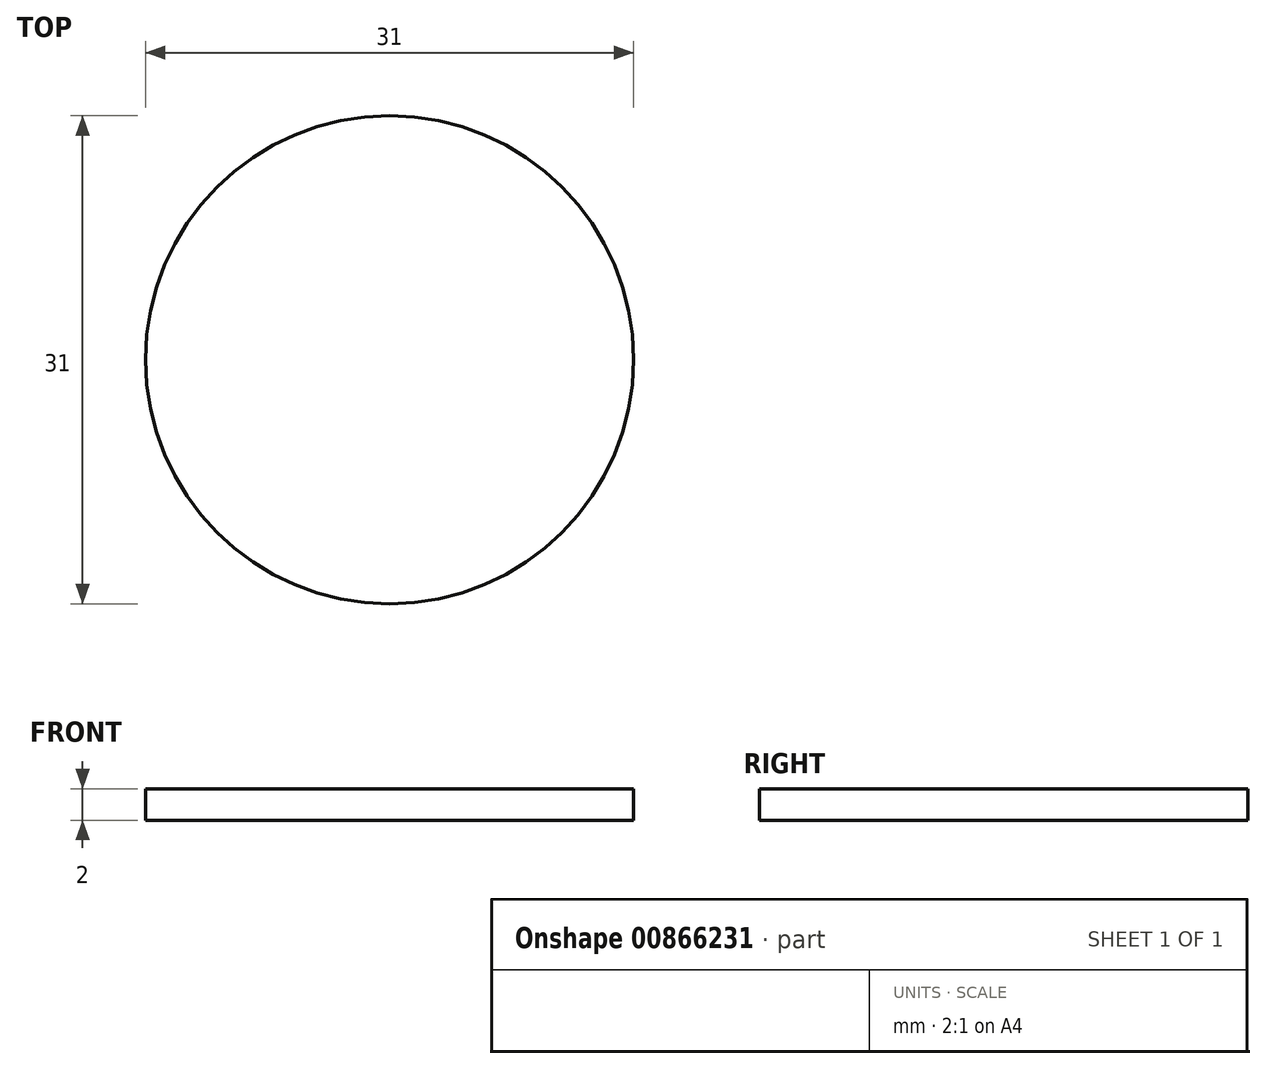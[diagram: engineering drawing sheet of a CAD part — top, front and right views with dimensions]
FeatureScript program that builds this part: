
annotation { "Feature Type Name" : "Feature", "Feature Type Description" : "" }
export const myFeature = defineFeature(function(context is Context, id is Id, definition is map)
    precondition{}
    {
        {
            var Q0;
            Q0=qCreatedBy(makeId("Top.planeOp"),FACE);
            var sketch = newSketch(context, id + "F0", { "sketchPlane" : qUnion([Q0])});
            skCircle(sketch, "E0", {"center": v(0, 0) * mm, "radius": 15.5 * mm});
            skSolve(sketch);
        }
        {
            var Q0;
            Q0 = qSketchRegion(id + "F0", true);
            extrude(context, id + "F1", {"entities" : qUnion([Q0]), "depth" : 2 * mm, "offsetDistance" : 25 * mm});
        }
        {
            var Q0;
            Q0=qCreatedBy(makeId("Top.planeOp"),FACE);
            var sketch = newSketch(context, id + "F2", { "sketchPlane" : qUnion([Q0])});
            skCircle(sketch, "E1", {"center": v(0, 0) * mm, "radius": 13 * mm});
            skSolve(sketch);
        }
        {
            var Q0;
            Q0=sQuery(id+"F2.wireOp",EDGE,"E1");
            extrude(context, id + "F3", {"bodyType" : ToolBodyType.SURFACE, "surfaceEntities" : qUnion([Q0]), "depth" : -2.5 * mm, "offsetDistance" : 25 * mm});
        }
    });
